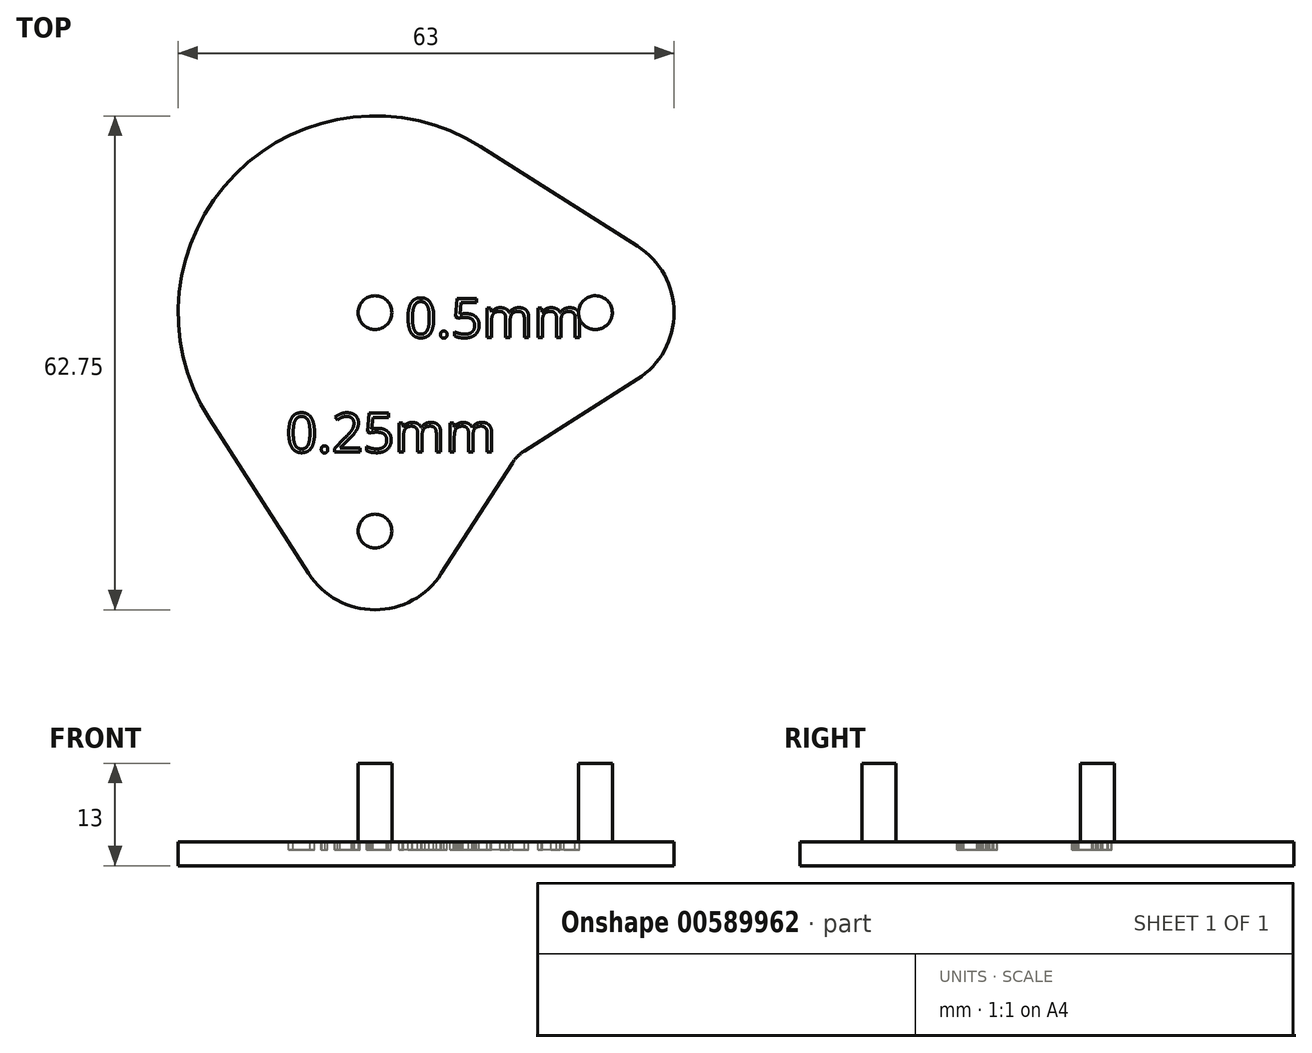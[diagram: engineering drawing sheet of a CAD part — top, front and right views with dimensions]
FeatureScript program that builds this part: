
annotation { "Feature Type Name" : "Feature", "Feature Type Description" : "" }
export const myFeature = defineFeature(function(context is Context, id is Id, definition is map)
    precondition{}
    {
        {
            var Q0;
            Q0=qCreatedBy(makeId("Top.planeOp"),FACE);
            var sketch = newSketch(context, id + "F0", { "sketchPlane" : qUnion([Q0])});
            skCircle(sketch, "E0", {"center": v(-33.75, 0) * mm, "radius": 25 * mm});
            skLineSegment(sketch, "E1", {"start": v(-33.75, 0) * mm, "end": v(-5.75, 0) * mm});
            skCircle(sketch, "E2", {"center": v(-5.75, 0) * mm, "radius": 10 * mm});
            skLineSegment(sketch, "E3", {"start": v(-14.76, -17.56) * mm, "end": v(-0.39, -8.44) * mm});
            skLineSegment(sketch, "E4", {"start": v(-20.35, 21.1) * mm, "end": v(-0.39, 8.44) * mm});
            skCircle(sketch, "E5", {"center": v(-33.75, -27.75) * mm, "radius": 10 * mm});
            skLineSegment(sketch, "E6", {"start": v(-33.75, -27.75) * mm, "end": v(-33.75, 0) * mm});
            skLineSegment(sketch, "E7", {"start": v(-25.33, -33.16) * mm, "end": v(-16.3, -19.08) * mm});
            skLineSegment(sketch, "E8", {"start": v(-42.16, -33.16) * mm, "end": v(-54.78, -13.51) * mm});
            skCircle(sketch, "E9", {"center": v(-33.75, -27.75) * mm, "radius": 2.25 * mm});
            skCircle(sketch, "E10", {"center": v(-5.75, 0) * mm, "radius": 2.25 * mm});
            skCircle(sketch, "E11", {"center": v(-33.75, 0) * mm, "radius": 2.25 * mm});
            skArc(sketch, "E12.filletArc", {"start": v(-14.76, -17.56) * mm, "mid": v(-15.61, -18.24) * mm, "end": v(-16.3, -19.08) * mm});
            skSolve(sketch);
        }
        {
            var Q0;
            Q0 = qSketchRegion(id + "F0", true);
            var Q1;
            {var subQ0=sQuery(id+"F0.wireOp",EDGE,"E1");var subQ1=sQuery(id+"F0.wireOp",EDGE,"E0");var subQ2=makeQuery(id+"F0.imprint","INTERSECT",VERTEX,{"derivedFrom":[subQ1,subQ0]});Q1=makeQuery(id+"F0.imprint","IMPRINT",FACE,{"disambiguationData":[TD([[makeQuery(id+"F0.imprint","IMPRINT",EDGE,{"disambiguationData":[TD([[subQ2,1.0]])],"derivedFrom":subQ1}),1.0]])]});}
            var Q2;
            Q2=makeQuery(id+"F0.imprint","IMPRINT",FACE,{"disambiguationData":[TD([[makeQuery(id+"F0.imprint","IMPRINT",EDGE,{"derivedFrom":sQuery(id+"F0.wireOp",EDGE,"E9")}),1.0]])]});
            var Q3;
            {var subQ0=sQuery(id+"F0.wireOp",EDGE,"E6");var subQ1=sQuery(id+"F0.wireOp",EDGE,"E1");var subQ2=makeQuery(id+"F0.imprint","INTERSECT",VERTEX,{"derivedFrom":[subQ1,subQ0]});Q3=makeQuery(id+"F0.imprint","IMPRINT",FACE,{"disambiguationData":[TD([[makeQuery(id+"F0.imprint","IMPRINT",EDGE,{"disambiguationData":[TD([[subQ2,-1.0]])],"derivedFrom":subQ1}),-1.0]])]});}
            var Q4;
            {var subQ0=sQuery(id+"F0.wireOp",EDGE,"E6");var subQ1=sQuery(id+"F0.wireOp",EDGE,"E1");var subQ2=makeQuery(id+"F0.imprint","INTERSECT",VERTEX,{"derivedFrom":[subQ1,subQ0]});Q4=makeQuery(id+"F0.imprint","IMPRINT",FACE,{"disambiguationData":[TD([[makeQuery(id+"F0.imprint","IMPRINT",EDGE,{"disambiguationData":[TD([[subQ2,-1.0]])],"derivedFrom":subQ1}),1.0]])]});}
            var Q5;
            Q5=makeQuery(id+"F0.imprint","IMPRINT",FACE,{"disambiguationData":[TD([[makeQuery(id+"F0.imprint","IMPRINT",EDGE,{"derivedFrom":sQuery(id+"F0.wireOp",EDGE,"E10")}),1.0]])]});
            var Q6;
            {var subQ0=sQuery(id+"F0.wireOp",EDGE,"E0");var subQ4=makeQuery(id+"F0.imprint","INTERSECT",VERTEX,{"derivedFrom":[subQ0,sQuery(id+"F0.wireOp",EDGE,"E3")]});Q6=makeQuery(id+"F0.imprint","IMPRINT",FACE,{"disambiguationData":[TD([[makeQuery(id+"F0.imprint","IMPRINT",EDGE,{"disambiguationData":[TD([[subQ4,1.0]])],"derivedFrom":subQ0}),1.0]])]});}
            var Q7;
            {var subQ0=sQuery(id+"F0.wireOp",EDGE,"E6");var subQ1=sQuery(id+"F0.wireOp",EDGE,"E0");var subQ2=makeQuery(id+"F0.imprint","INTERSECT",VERTEX,{"derivedFrom":[subQ1,subQ0]});Q7=makeQuery(id+"F0.imprint","IMPRINT",FACE,{"disambiguationData":[TD([[makeQuery(id+"F0.imprint","IMPRINT",EDGE,{"disambiguationData":[TD([[subQ2,-1.0]])],"derivedFrom":subQ1}),1.0]])]});}
            var Q8;
            {var subQ0=sQuery(id+"F0.wireOp",EDGE,"E6");var subQ1=sQuery(id+"F0.wireOp",EDGE,"E0");var subQ2=makeQuery(id+"F0.imprint","INTERSECT",VERTEX,{"derivedFrom":[subQ1,subQ0]});Q8=makeQuery(id+"F0.imprint","IMPRINT",FACE,{"disambiguationData":[TD([[makeQuery(id+"F0.imprint","IMPRINT",EDGE,{"disambiguationData":[TD([[subQ2,1.0]])],"derivedFrom":subQ1}),1.0]])]});}
            var Q9;
            {var subQ0=sQuery(id+"F0.wireOp",EDGE,"E1");var subQ1=sQuery(id+"F0.wireOp",EDGE,"E0");var subQ2=makeQuery(id+"F0.imprint","INTERSECT",VERTEX,{"derivedFrom":[subQ1,subQ0]});Q9=makeQuery(id+"F0.imprint","IMPRINT",FACE,{"disambiguationData":[TD([[makeQuery(id+"F0.imprint","IMPRINT",EDGE,{"disambiguationData":[TD([[subQ2,-1.0]])],"derivedFrom":subQ1}),1.0]])]});}
            var Q10;
            {var subQ0=sQuery(id+"F0.wireOp",EDGE,"E5");var subQ1=sQuery(id+"F0.wireOp",EDGE,"E0");var subQ2=makeQuery(id+"F0.imprint","INTERSECT",VERTEX,{"disambiguationData":[OD(1.0)],"derivedFrom":[subQ1,subQ0]});Q10=makeQuery(id+"F0.imprint","IMPRINT",FACE,{"disambiguationData":[TD([[makeQuery(id+"F0.imprint","IMPRINT",EDGE,{"disambiguationData":[TD([[subQ2,-1.0]])],"derivedFrom":subQ1}),1.0]])]});}
            extrude(context, id + "F1", {"entities" : qUnion([Q0, Q1, Q2, Q3, Q4, Q5, Q6, Q7, Q8, Q9, Q10]), "depth" : 3 * mm, "offsetDistance" : 25 * mm});
        }
        {
            var Q0;
            Q0=makeQuery(id+"F1.opExtrude","CAP_FACE",FACE,{"disambiguationData":[OSD([sQuery(id+"F0.wireOp",EDGE,"E0"),sQuery(id+"F0.wireOp",EDGE,"E2"),sQuery(id+"F0.wireOp",EDGE,"E3"),sQuery(id+"F0.wireOp",EDGE,"E4"),sQuery(id+"F0.wireOp",EDGE,"E5"),sQuery(id+"F0.wireOp",EDGE,"E7"),sQuery(id+"F0.wireOp",EDGE,"E8"),sQuery(id+"F0.wireOp",EDGE,"21661166-374e-414a-a767-4ed40ed9ffe5.filletArc")])],"isStart":false});
            var sketch = newSketch(context, id + "F2", { "sketchPlane" : qUnion([Q0])});
            skSolve(sketch);
        }
        {
            var Q0;
            Q0=makeQuery(id+"F2.imprint","IMPRINT",FACE,{"disambiguationData":[TD([[makeQuery(id+"F2.imprint","IMPRINT",EDGE,{"derivedFrom":makeQuery(id+"F1.opExtrude","CAP_EDGE",EDGE,{"disambiguationData":[OSD([sQuery(id+"F0.wireOp",EDGE,"E0")])],"isStart":false})}),1.0]])]});
            var sketch = newSketch(context, id + "F3", { "sketchPlane" : qUnion([Q0])});
            skCircle(sketch, "E13", {"center": v(-33.75, -27.75) * mm, "radius": 2.15 * mm});
            skCircle(sketch, "E14", {"center": v(-5.75, 0) * mm, "radius": 2.15 * mm});
            skCircle(sketch, "E15", {"center": v(-33.75, 0) * mm, "radius": 2.15 * mm});
            skSolve(sketch);
        }
        {
            var Q0;
            Q0 = qSketchRegion(id + "F3", true);
            extrude(context, id + "F4", {"entities" : qUnion([Q0]), "operationType" : NewBodyOperationType.ADD, "depth" : 10 * mm, "offsetDistance" : 25 * mm});
        }
        {
            var Q0;
            Q0=makeQuery(id+"F2.imprint","IMPRINT",FACE,{"disambiguationData":[TD([[makeQuery(id+"F2.imprint","IMPRINT",EDGE,{"derivedFrom":makeQuery(id+"F1.opExtrude","CAP_EDGE",EDGE,{"disambiguationData":[OSD([sQuery(id+"F0.wireOp",EDGE,"E0")])],"isStart":false})}),1.0]])]});
            var sketch = newSketch(context, id + "F5", { "sketchPlane" : qUnion([Q0])});
            skText(sketch, "E16", { "text": "0.5mm", "fontName": "OpenSans-Regular.ttf"});
            skText(sketch, "E17", { "text": "0.25mm", "fontName": "OpenSans-Regular.ttf"});
            const initialGuessF5  = {"E16": [-0.0299, -0.00315, 1, 0, 0.005], "E17": [-0.04505, -0.01773, 1, 0, 0.005]};
            skSetInitialGuess(sketch, initialGuessF5);
            skSolve(sketch);
        }
        {
            var Q0;
            Q0 = qSketchRegion(id + "F5", true);
            extrude(context, id + "F6", {"entities" : qUnion([Q0]), "operationType" : NewBodyOperationType.REMOVE, "depth" : -1 * mm, "offsetDistance" : 25 * mm});
        }
    });
